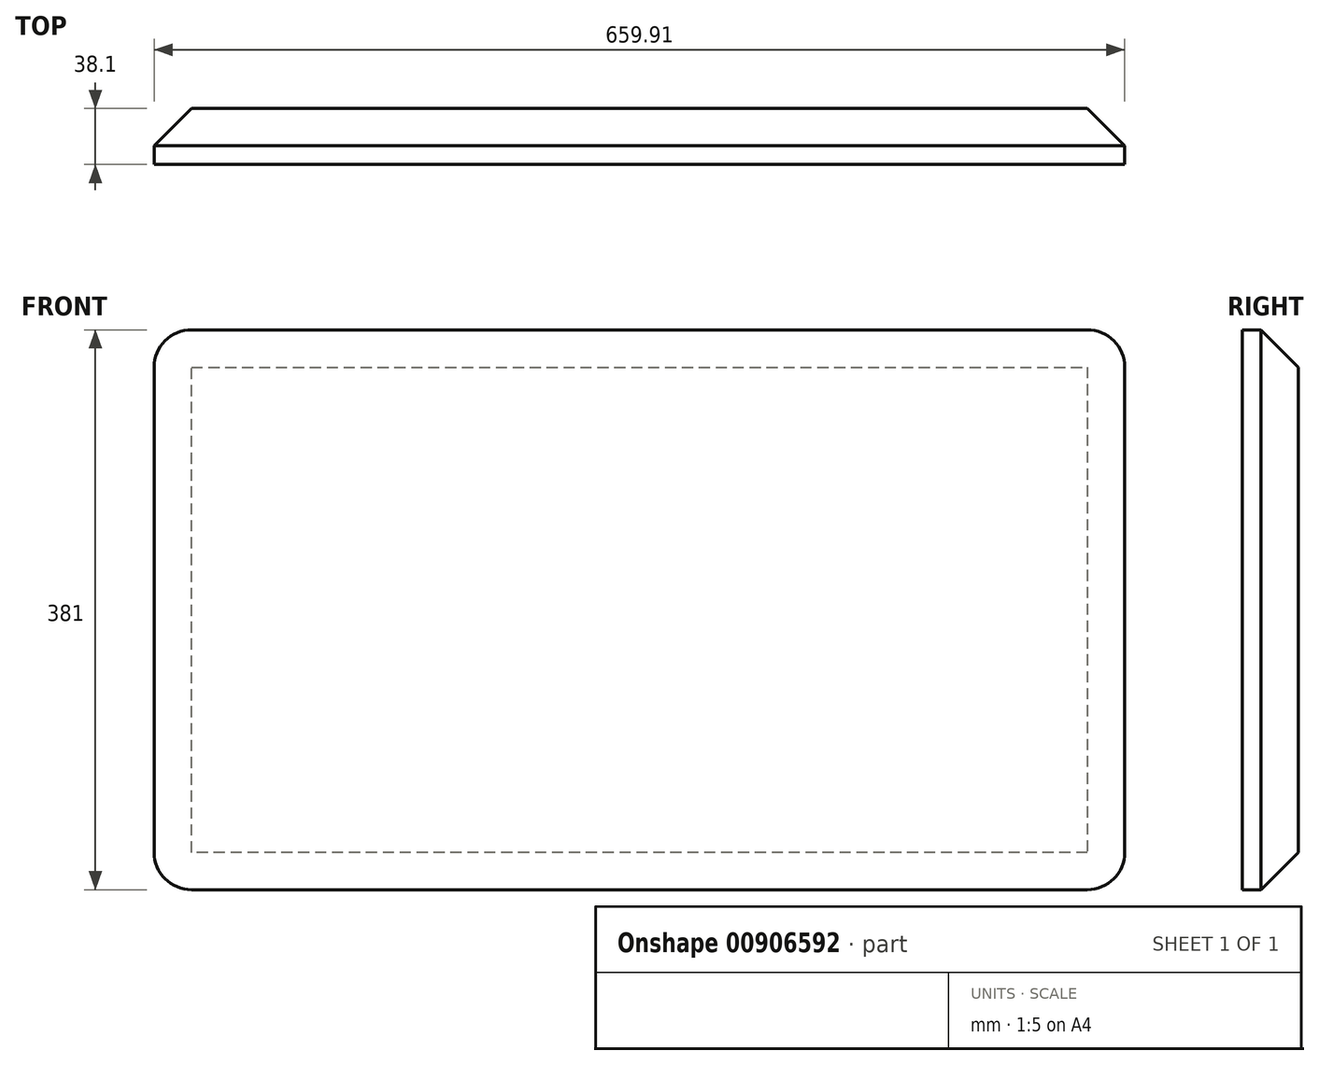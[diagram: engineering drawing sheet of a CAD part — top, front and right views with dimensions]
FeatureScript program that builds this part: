
annotation { "Feature Type Name" : "Feature", "Feature Type Description" : "" }
export const myFeature = defineFeature(function(context is Context, id is Id, definition is map)
    precondition{}
    {
        {
            var Q0;
            Q0=qCreatedBy(makeId("Front.planeOp"),FACE);
            var sketch = newSketch(context, id + "F0", { "sketchPlane" : qUnion([Q0])});
            skLineSegment(sketch, "E0.bottom", {"start": v(0, 0) * mm, "end": v(-659.91, 0) * mm});
            skLineSegment(sketch, "E0.top", {"start": v(0, 381) * mm, "end": v(-659.91, 381) * mm});
            skLineSegment(sketch, "E0.left", {"start": v(0, 0) * mm, "end": v(0, 381) * mm});
            skLineSegment(sketch, "E0.right", {"start": v(-659.91, 0) * mm, "end": v(-659.91, 381) * mm});
            skLineSegment(sketch, "E1", {"start": v(-659.91, 381) * mm, "end": v(0, 0) * mm});
            skSolve(sketch);
        }
        {
            var Q0;
            Q0=makeQuery(id+"F0.imprint","IMPRINT",FACE,{"disambiguationData":[TD([[makeQuery(id+"F0.imprint","IMPRINT",EDGE,{"derivedFrom":sQuery(id+"F0.wireOp",EDGE,"E0.bottom")}),-1.0]])]});
            var Q1;
            Q1=makeQuery(id+"F0.imprint","IMPRINT",FACE,{"disambiguationData":[TD([[makeQuery(id+"F0.imprint","IMPRINT",EDGE,{"derivedFrom":sQuery(id+"F0.wireOp",EDGE,"E0.top")}),1.0]])]});
            extrude(context, id + "F1", {"entities" : qUnion([Q0, Q1]), "depth" : 38.1 * mm, "offsetDistance" : 25.4 * mm});
        }
        {
            var Q0;
            Q0=makeQuery(id+"F1.opExtrude","SWEPT_EDGE",EDGE,{"disambiguationData":[OSD([sQuery(id+"F0.wireOp",EDGE,"E0.top"),sQuery(id+"F0.wireOp",EDGE,"E0.right"),sQuery(id+"F0.wireOp",EDGE,"E1")])]});
            var Q1;
            Q1=makeQuery(id+"F1.opExtrude","SWEPT_EDGE",EDGE,{"disambiguationData":[OSD([sQuery(id+"F0.wireOp",EDGE,"E0.top"),sQuery(id+"F0.wireOp",EDGE,"E0.left")])]});
            var Q2;
            Q2=makeQuery(id+"F1.opExtrude","SWEPT_EDGE",EDGE,{"disambiguationData":[OSD([sQuery(id+"F0.wireOp",EDGE,"E0.bottom"),sQuery(id+"F0.wireOp",EDGE,"E0.left"),sQuery(id+"F0.wireOp",EDGE,"E1")])]});
            var Q3;
            Q3=makeQuery(id+"F1.opExtrude","SWEPT_EDGE",EDGE,{"disambiguationData":[OSD([sQuery(id+"F0.wireOp",EDGE,"E0.bottom"),sQuery(id+"F0.wireOp",EDGE,"E0.right")])]});
            fillet(context, id + "F2", {"entities" : qUnion([Q0, Q1, Q2, Q3]), "radius" : 25.4 * mm, "tangentPropagation" : true, "allowEdgeOverflow" : false});
        }
        {
            var Q0;
            Q0=makeQuery(id+"F1.opExtrude","CAP_FACE",FACE,{"disambiguationData":[OSD([sQuery(id+"F0.wireOp",EDGE,"E0.bottom"),sQuery(id+"F0.wireOp",EDGE,"E0.top"),sQuery(id+"F0.wireOp",EDGE,"E0.left"),sQuery(id+"F0.wireOp",EDGE,"E0.right")])],"isStart":true});
            chamfer(context, id + "F3", {"entities" : qUnion([Q0]), "width" : 25.4 * mm, "tangentPropagation" : true});
        }
    });
